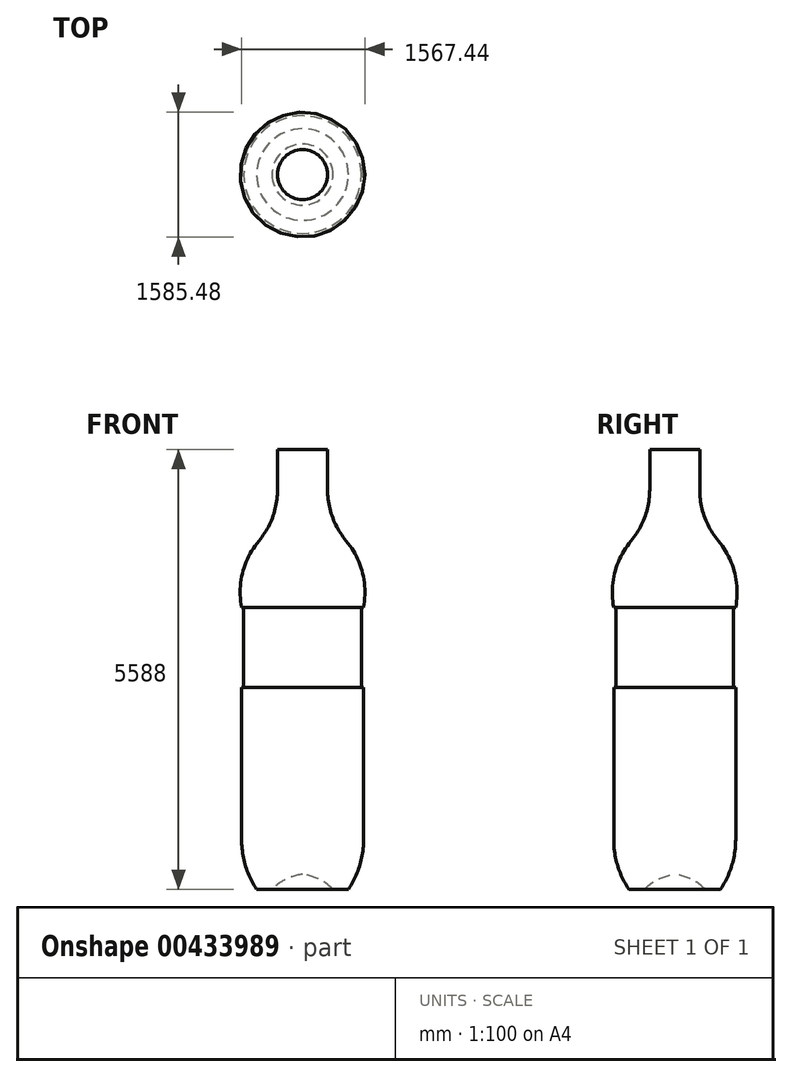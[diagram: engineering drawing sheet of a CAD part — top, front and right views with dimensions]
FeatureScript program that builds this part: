
annotation { "Feature Type Name" : "Feature", "Feature Type Description" : "" }
export const myFeature = defineFeature(function(context is Context, id is Id, definition is map)
    precondition{}
    {
        {
            var Q0;
            Q0=qCreatedBy(makeId("Front.planeOp"),FACE);
            var sketch = newSketch(context, id + "F0", { "sketchPlane" : qUnion([Q0])});
            skLineSegment(sketch, "E0", {"start": v(0, 0) * mm, "end": v(0, -5397.5) * mm});
            skLineSegment(sketch, "E1", {"start": v(0, 0) * mm, "end": v(-317.5, 0) * mm});
            skLineSegment(sketch, "E2", {"start": v(-317.5, 0) * mm, "end": v(-317.5, -355.6) * mm});
            skLineSegment(sketch, "E3", {"start": v(-317.5, -355.6) * mm, "end": v(-317.5, -508) * mm});
            skArc(sketch, "E4", {"start": v(-555.12, -1160.98) * mm, "mid": v(-378.75, -855.43) * mm, "end": v(-317.5, -508) * mm});
            skLineSegment(sketch, "E5", {"start": v(0, -5397.5) * mm, "end": v(0, -5588) * mm});
            skLineSegment(sketch, "E6", {"start": v(0, -5588) * mm, "end": v(-774.7, -5588) * mm});
            skLineSegment(sketch, "E7", {"start": v(-774.7, -5588) * mm, "end": v(-774.7, -4953) * mm});
            skLineSegment(sketch, "E8", {"start": v(-774.7, -4953) * mm, "end": v(-774.7, -3020.57) * mm});
            skArc(sketch, "E9", {"start": v(0, -5397.5) * mm, "mid": v(-210.36, -5458.83) * mm, "end": v(-387.35, -5588) * mm});
            skArc(sketch, "E10", {"start": v(-582.08, -5588) * mm, "mid": v(-484.72, -5623.16) * mm, "end": v(-387.35, -5588) * mm});
            skArc(sketch, "E11", {"start": v(-774.7, -4953) * mm, "mid": v(-725.49, -5284.79) * mm, "end": v(-582.08, -5588) * mm});
            skArc(sketch, "E12", {"start": v(-555.12, -1160.98) * mm, "mid": v(-759.98, -1558.03) * mm, "end": v(-774.7, -2004.57) * mm});
            skLineSegment(sketch, "E13", {"start": v(-555.12, -1160.98) * mm, "end": v(-555.12, -1160.98) * mm});
            skLineSegment(sketch, "E14", {"start": v(-774.7, -3206.48) * mm, "end": v(-746.76, -3206.48) * mm});
            skLineSegment(sketch, "E15", {"start": v(-774.7, -3020.57) * mm, "end": v(-746.76, -3020.57) * mm});
            skLineSegment(sketch, "E16", {"start": v(-746.76, -3020.57) * mm, "end": v(-746.76, -2004.57) * mm});
            skLineSegment(sketch, "E17", {"start": v(-746.76, -2004.57) * mm, "end": v(-774.7, -2004.57) * mm});
            skSolve(sketch);
        }
        {
            var Q0;
            Q0=makeQuery(id+"F0.imprint","IMPRINT",FACE,{"disambiguationData":[TD([[makeQuery(id+"F0.imprint","IMPRINT",EDGE,{"derivedFrom":sQuery(id+"F0.wireOp",EDGE,"E0")}),-1.0]])]});
            var Q1;
            Q1=sQuery(id+"F0.wireOp",EDGE,"E0");
            revolve(context, id + "F1", {"entities" : qUnion([Q0]), "axis" : qUnion([Q1]), "revolveType" : RevolveType.FULL});
        }
    });
